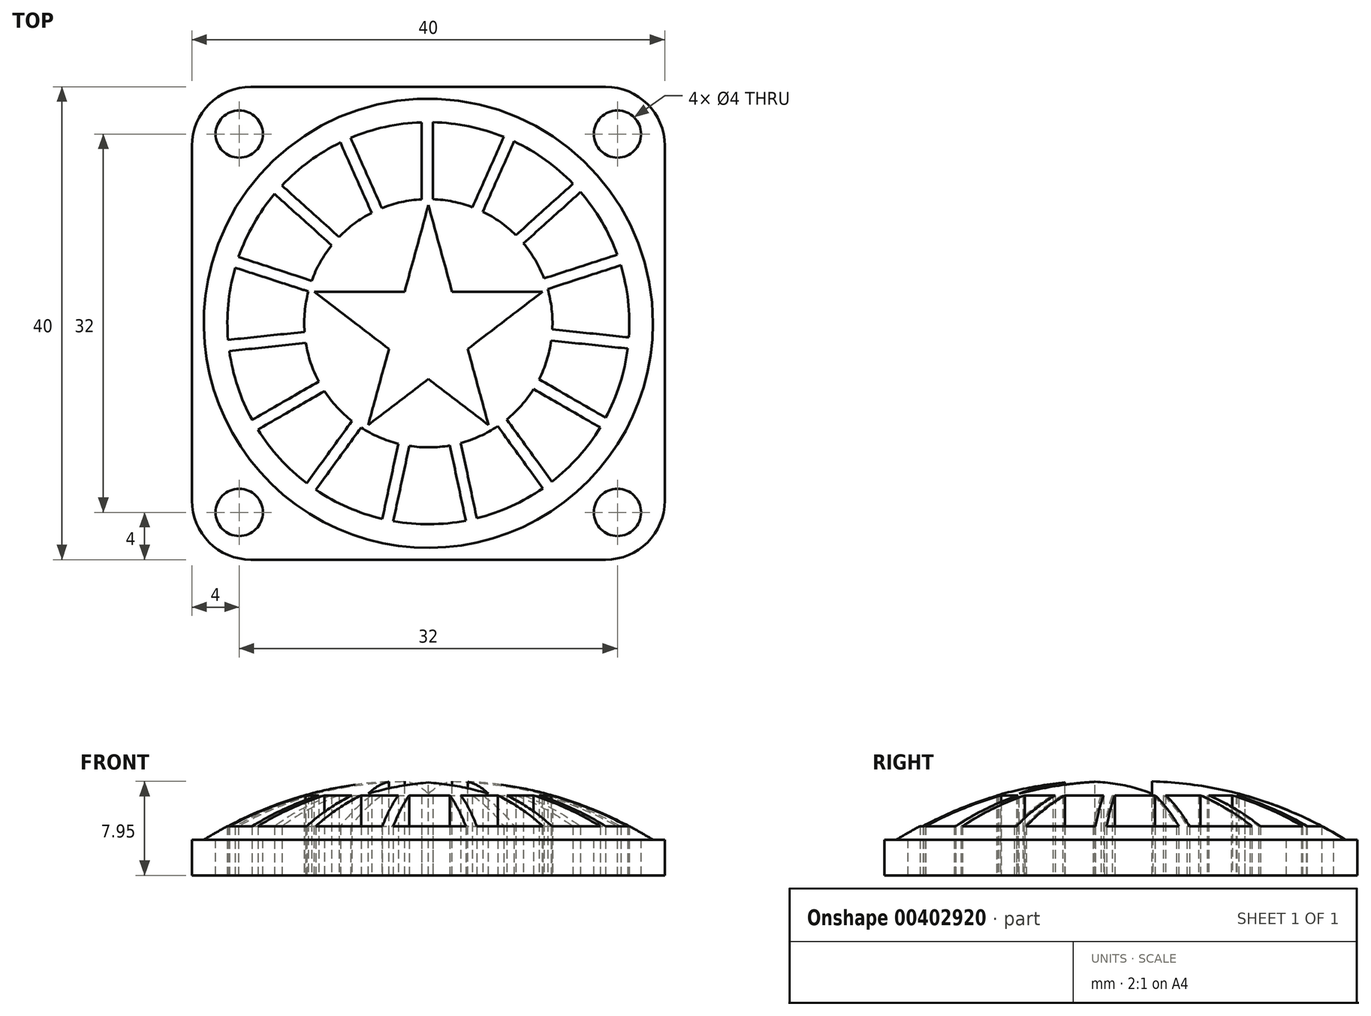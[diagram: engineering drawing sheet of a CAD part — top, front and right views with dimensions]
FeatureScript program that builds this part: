
annotation { "Feature Type Name" : "Feature", "Feature Type Description" : "" }
export const myFeature = defineFeature(function(context is Context, id is Id, definition is map)
    precondition{}
    {
        {
            var Q0;
            Q0=qCreatedBy(makeId("Top.planeOp"),FACE);
            var sketch = newSketch(context, id + "F0", { "sketchPlane" : qUnion([Q0])});
            skLineSegment(sketch, "E0.bottom", {"start": v(0, 0) * mm, "end": v(40, 0) * mm});
            skLineSegment(sketch, "E0.top", {"start": v(0, 40) * mm, "end": v(40, 40) * mm});
            skLineSegment(sketch, "E0.left", {"start": v(0, 0) * mm, "end": v(0, 40) * mm});
            skLineSegment(sketch, "E0.right", {"start": v(40, 0) * mm, "end": v(40, 40) * mm});
            skSolve(sketch);
        }
        {
            var Q0;
            Q0 = qSketchRegion(id + "F0", true);
            extrude(context, id + "F1", {"entities" : qUnion([Q0]), "depth" : 3 * mm, "offsetDistance" : 25 * mm});
        }
        {
            var Q0;
            Q0=makeQuery(id+"F1.opExtrude","CAP_FACE",FACE,{"disambiguationData":[OSD([sQuery(id+"F0.wireOp",EDGE,"E0.bottom"),sQuery(id+"F0.wireOp",EDGE,"E0.top"),sQuery(id+"F0.wireOp",EDGE,"E0.left"),sQuery(id+"F0.wireOp",EDGE,"E0.right")])],"isStart":false});
            var sketch = newSketch(context, id + "F2", { "sketchPlane" : qUnion([Q0])});
            skCircle(sketch, "E1", {"center": v(4, 36) * mm, "radius": 2 * mm});
            skCircle(sketch, "E2", {"center": v(36, 36) * mm, "radius": 2 * mm});
            skCircle(sketch, "E3", {"center": v(36, 4) * mm, "radius": 2 * mm});
            skCircle(sketch, "E4", {"center": v(4, 4) * mm, "radius": 2 * mm});
            skSolve(sketch);
        }
        {
            var Q0;
            Q0 = qSketchRegion(id + "F2", true);
            extrude(context, id + "F3", {"entities" : qUnion([Q0]), "operationType" : NewBodyOperationType.REMOVE, "oppositeDirection" : true, "depth" : 25 * mm, "offsetDistance" : 25 * mm});
        }
        {
            var Q0;
            Q0=makeQuery(id+"F1.opExtrude","CAP_FACE",FACE,{"disambiguationData":[OSD([sQuery(id+"F0.wireOp",EDGE,"E0.bottom"),sQuery(id+"F0.wireOp",EDGE,"E0.top"),sQuery(id+"F0.wireOp",EDGE,"E0.left"),sQuery(id+"F0.wireOp",EDGE,"E0.right")])],"isStart":false});
            var sketch = newSketch(context, id + "F4", { "sketchPlane" : qUnion([Q0])});
            skCircle(sketch, "E5", {"center": v(20, 20) * mm, "radius": 19 * mm});
            skPoint(sketch, "E5.centerSnap0", {"position": v(40, 20) * mm});
            skPoint(sketch, "E5.centerSnap1", {"position": v(20, 40) * mm});
            skSolve(sketch);
        }
        {
            var Q0;
            Q0 = qSketchRegion(id + "F4", true);
            extrude(context, id + "F5", {"entities" : qUnion([Q0]), "operationType" : NewBodyOperationType.ADD, "depth" : 5 * mm, "offsetDistance" : 25 * mm});
        }
        {
            var Q0;
            Q0=makeQuery(id+"F5.opExtrude","CAP_EDGE",EDGE,{"disambiguationData":[OSD([sQuery(id+"F4.wireOp",EDGE,"E5")])],"isStart":false});
            fillet(context, id + "F6", {"entities" : qUnion([Q0]), "radius" : 33 * mm, "tangentPropagation" : true, "allowEdgeOverflow" : false});
        }
        {
            var Q0;
            Q0=makeQuery(id+"F5.opExtrude","CAP_FACE",FACE,{"disambiguationData":[OSD([sQuery(id+"F4.wireOp",EDGE,"E5")])],"isStart":false});
            var sketch = newSketch(context, id + "F7", { "sketchPlane" : qUnion([Q0])});
            skLineSegment(sketch, "E6", {"start": v(20, 30) * mm, "end": v(17.99, 22.65) * mm});
            skLineSegment(sketch, "E7", {"start": v(25.1, 11.4) * mm, "end": v(20, 15.28) * mm});
            skLineSegment(sketch, "E8", {"start": v(10.36, 22.65) * mm, "end": v(17.99, 22.65) * mm});
            skLineSegment(sketch, "E9", {"start": v(29.64, 22.65) * mm, "end": v(23.33, 17.83) * mm});
            skLineSegment(sketch, "E10", {"start": v(20, 30) * mm, "end": v(22.01, 22.65) * mm});
            skLineSegment(sketch, "E11.trimOffspring", {"start": v(22.01, 22.65) * mm, "end": v(29.64, 22.65) * mm});
            skLineSegment(sketch, "E12.trimOffspring", {"start": v(16.67, 17.83) * mm, "end": v(14.9, 11.4) * mm});
            skLineSegment(sketch, "E13.trimOffspring", {"start": v(16.67, 17.83) * mm, "end": v(10.36, 22.65) * mm});
            skLineSegment(sketch, "E14.trimOffspring", {"start": v(20, 15.28) * mm, "end": v(14.9, 11.4) * mm});
            skLineSegment(sketch, "E15.trimOffspring", {"start": v(23.33, 17.83) * mm, "end": v(25.1, 11.4) * mm});
            skPoint(sketch, "E16.center.orphan", {"position": v(20, 20) * mm});
            skSolve(sketch);
        }
        {
            var Q0;
            Q0 = qSketchRegion(id + "F7", true);
            extrude(context, id + "F8", {"entities" : qUnion([Q0]), "operationType" : NewBodyOperationType.REMOVE, "oppositeDirection" : true, "depth" : 25 * mm, "offsetDistance" : 25 * mm});
        }
        {
            var Q0;
            Q0=makeQuery(id+"F1.opExtrude","CAP_FACE",FACE,{"disambiguationData":[OSD([sQuery(id+"F0.wireOp",EDGE,"E0.bottom"),sQuery(id+"F0.wireOp",EDGE,"E0.top"),sQuery(id+"F0.wireOp",EDGE,"E0.left"),sQuery(id+"F0.wireOp",EDGE,"E0.right")])],"isStart":true});
            var sketch = newSketch(context, id + "F9", { "sketchPlane" : qUnion([Q0])});
            skArc(sketch, "E17", {"start": v(20.37, -30.5) * mm, "mid": v(22.08, -30.3) * mm, "end": v(23.73, -29.81) * mm});
            skPoint(sketch, "E17.centerSnap0", {"position": v(20, -40) * mm});
            skPoint(sketch, "E17.centerSnap1", {"position": v(0, -20) * mm});
            skArc(sketch, "E18", {"start": v(20.37, -37) * mm, "mid": v(23.43, -36.65) * mm, "end": v(26.38, -35.76) * mm});
            skLineSegment(sketch, "E19.left", {"start": v(20.37, -37) * mm, "end": v(20.37, -30.48) * mm});
            skLineSegment(sketch, "E19.right", {"start": v(19.42, -37) * mm, "end": v(19.42, -30.48) * mm});
            skLineSegment(sketch, "E20.1.0", {"start": v(27.25, -35.38) * mm, "end": v(24.6, -29.43) * mm});
            skLineSegment(sketch, "E20.1.1", {"start": v(26.38, -35.76) * mm, "end": v(23.73, -29.81) * mm});
            skLineSegment(sketch, "E20.2.0", {"start": v(32.88, -31.1) * mm, "end": v(28.04, -26.74) * mm});
            skLineSegment(sketch, "E20.2.1", {"start": v(32.24, -31.8) * mm, "end": v(27.4, -27.45) * mm});
            skLineSegment(sketch, "E20.3.0", {"start": v(36.28, -24.9) * mm, "end": v(30.08, -22.89) * mm});
            skLineSegment(sketch, "E20.3.1", {"start": v(35.98, -25.8) * mm, "end": v(29.8, -23.8) * mm});
            skLineSegment(sketch, "E20.3.2", {"start": v(30.08, -22.89) * mm, "end": v(29.8, -23.8) * mm});
            skLineSegment(sketch, "E20.4.0", {"start": v(36.86, -17.86) * mm, "end": v(30.39, -18.54) * mm});
            skLineSegment(sketch, "E20.4.1", {"start": v(36.96, -18.8) * mm, "end": v(30.49, -19.48) * mm});
            skLineSegment(sketch, "E20.5.0", {"start": v(34.53, -11.18) * mm, "end": v(28.9, -14.44) * mm});
            skLineSegment(sketch, "E20.5.1", {"start": v(35, -12) * mm, "end": v(29.37, -15.26) * mm});
            skLineSegment(sketch, "E20.6.0", {"start": v(29.7, -6.03) * mm, "end": v(25.86, -11.3) * mm});
            skLineSegment(sketch, "E20.6.1", {"start": v(30.46, -6.6) * mm, "end": v(26.63, -11.86) * mm});
            skLineSegment(sketch, "E20.7.0", {"start": v(23.17, -3.3) * mm, "end": v(21.82, -9.67) * mm});
            skLineSegment(sketch, "E20.7.1", {"start": v(24.1, -3.5) * mm, "end": v(22.75, -9.87) * mm});
            skLineSegment(sketch, "E20.8.0", {"start": v(16.1, -3.45) * mm, "end": v(17.46, -9.82) * mm});
            skLineSegment(sketch, "E20.8.1", {"start": v(17.04, -3.26) * mm, "end": v(18.39, -9.62) * mm});
            skLineSegment(sketch, "E20.9.0", {"start": v(9.71, -6.47) * mm, "end": v(13.54, -11.74) * mm});
            skLineSegment(sketch, "E20.9.1", {"start": v(10.48, -5.91) * mm, "end": v(14.3, -11.18) * mm});
            skLineSegment(sketch, "E20.10.0", {"start": v(5.1, -11.82) * mm, "end": v(10.74, -15.08) * mm});
            skLineSegment(sketch, "E20.10.1", {"start": v(5.58, -11) * mm, "end": v(11.21, -14.25) * mm});
            skLineSegment(sketch, "E20.11.0", {"start": v(3.06, -18.6) * mm, "end": v(9.53, -19.27) * mm});
            skLineSegment(sketch, "E20.11.1", {"start": v(3.16, -17.65) * mm, "end": v(9.63, -18.33) * mm});
            skLineSegment(sketch, "E20.12.0", {"start": v(3.95, -25.6) * mm, "end": v(10.14, -23.6) * mm});
            skLineSegment(sketch, "E20.12.1", {"start": v(3.66, -24.7) * mm, "end": v(9.85, -22.69) * mm});
            skLineSegment(sketch, "E20.13.0", {"start": v(7.62, -31.65) * mm, "end": v(12.46, -27.29) * mm});
            skLineSegment(sketch, "E20.13.1", {"start": v(6.99, -30.94) * mm, "end": v(11.82, -26.58) * mm});
            skLineSegment(sketch, "E20.14.0", {"start": v(13.42, -35.68) * mm, "end": v(16.07, -29.73) * mm});
            skLineSegment(sketch, "E20.14.1", {"start": v(12.56, -35.28) * mm, "end": v(15.2, -29.34) * mm});
            skArc(sketch, "E21.trimOffspring", {"start": v(13.42, -35.68) * mm, "mid": v(16.36, -36.6) * mm, "end": v(19.42, -37) * mm});
            skArc(sketch, "E22.trimOffspring", {"start": v(16.07, -29.74) * mm, "mid": v(17.71, -30.25) * mm, "end": v(19.42, -30.48) * mm});
            skArc(sketch, "E23.trimOffspring", {"start": v(12.45, -27.3) * mm, "mid": v(13.74, -28.43) * mm, "end": v(15.2, -29.34) * mm});
            skArc(sketch, "E24.trimOffspring", {"start": v(7.62, -31.65) * mm, "mid": v(9.92, -33.7) * mm, "end": v(12.56, -35.28) * mm});
            skArc(sketch, "E25.trimOffspring", {"start": v(3.95, -25.6) * mm, "mid": v(5.22, -28.4) * mm, "end": v(6.99, -30.94) * mm});
            skArc(sketch, "E26.trimOffspring", {"start": v(10.13, -23.6) * mm, "mid": v(10.85, -25.16) * mm, "end": v(11.82, -26.58) * mm});
            skArc(sketch, "E27.trimOffspring", {"start": v(24.6, -29.44) * mm, "mid": v(26.09, -28.56) * mm, "end": v(27.4, -27.45) * mm});
            skArc(sketch, "E28.trimOffspring", {"start": v(27.25, -35.38) * mm, "mid": v(29.9, -33.82) * mm, "end": v(32.24, -31.8) * mm});
            skArc(sketch, "E29.trimOffspring", {"start": v(32.88, -31.1) * mm, "mid": v(34.67, -28.6) * mm, "end": v(35.98, -25.8) * mm});
            skArc(sketch, "E30.trimOffspring", {"start": v(28.05, -26.75) * mm, "mid": v(29.04, -25.34) * mm, "end": v(29.8, -23.8) * mm});
            skArc(sketch, "E31.trimOffspring", {"start": v(30.1, -22.9) * mm, "mid": v(30.43, -21.2) * mm, "end": v(30.49, -19.48) * mm});
            skArc(sketch, "E32.trimOffspring", {"start": v(36.28, -24.9) * mm, "mid": v(36.9, -21.88) * mm, "end": v(36.96, -18.8) * mm});
            skArc(sketch, "E33.trimOffspring", {"start": v(36.86, -17.86) * mm, "mid": v(36.2, -14.85) * mm, "end": v(35, -12) * mm});
            skArc(sketch, "E34.trimOffspring", {"start": v(30.4, -18.54) * mm, "mid": v(30.02, -16.86) * mm, "end": v(29.37, -15.26) * mm});
            skArc(sketch, "E35.trimOffspring", {"start": v(29.7, -6.03) * mm, "mid": v(27.01, -4.51) * mm, "end": v(24.1, -3.5) * mm});
            skArc(sketch, "E36.trimOffspring", {"start": v(34.53, -11.18) * mm, "mid": v(32.7, -8.7) * mm, "end": v(30.46, -6.6) * mm});
            skArc(sketch, "E37.trimOffspring", {"start": v(28.9, -14.43) * mm, "mid": v(27.87, -13.05) * mm, "end": v(26.63, -11.86) * mm});
            skArc(sketch, "E38.trimOffspring", {"start": v(25.87, -11.3) * mm, "mid": v(24.37, -10.45) * mm, "end": v(22.75, -9.87) * mm});
            skArc(sketch, "E39.trimOffspring", {"start": v(21.82, -9.66) * mm, "mid": v(20.1, -9.5) * mm, "end": v(18.39, -9.62) * mm});
            skArc(sketch, "E40.trimOffspring", {"start": v(23.17, -3.3) * mm, "mid": v(20.1, -3) * mm, "end": v(17.04, -3.26) * mm});
            skArc(sketch, "E41.trimOffspring", {"start": v(16.1, -3.45) * mm, "mid": v(13.18, -4.43) * mm, "end": v(10.48, -5.91) * mm});
            skArc(sketch, "E42.trimOffspring", {"start": v(17.46, -9.81) * mm, "mid": v(15.83, -10.37) * mm, "end": v(14.3, -11.18) * mm});
            skArc(sketch, "E43.trimOffspring", {"start": v(13.53, -11.73) * mm, "mid": v(12.27, -12.9) * mm, "end": v(11.21, -14.25) * mm});
            skArc(sketch, "E44.trimOffspring", {"start": v(9.71, -6.47) * mm, "mid": v(7.44, -8.55) * mm, "end": v(5.58, -11) * mm});
            skArc(sketch, "E45.trimOffspring", {"start": v(5.1, -11.82) * mm, "mid": v(3.87, -14.65) * mm, "end": v(3.16, -17.65) * mm});
            skArc(sketch, "E46.trimOffspring", {"start": v(10.73, -15.07) * mm, "mid": v(10.05, -16.65) * mm, "end": v(9.63, -18.33) * mm});
            skArc(sketch, "E47.trimOffspring", {"start": v(9.53, -19.27) * mm, "mid": v(9.55, -21) * mm, "end": v(9.85, -22.69) * mm});
            skArc(sketch, "E48.trimOffspring", {"start": v(3.06, -18.6) * mm, "mid": v(3.08, -21.67) * mm, "end": v(3.66, -24.7) * mm});
            skSolve(sketch);
        }
        {
            var Q0;
            Q0 = qSketchRegion(id + "F9", true);
            extrude(context, id + "F10", {"entities" : qUnion([Q0]), "operationType" : NewBodyOperationType.REMOVE, "oppositeDirection" : true, "depth" : 25 * mm, "offsetDistance" : 25 * mm});
        }
        {
            var Q0;
            Q0=makeQuery(id+"F1.opExtrude","SWEPT_EDGE",EDGE,{"disambiguationData":[OSD([sQuery(id+"F0.wireOp",EDGE,"E0.top"),sQuery(id+"F0.wireOp",EDGE,"E0.left")])]});
            fillet(context, id + "F11", {"entities" : qUnion([Q0]), "radius" : 5 * mm, "tangentPropagation" : true, "allowEdgeOverflow" : false});
        }
        {
            var Q0;
            Q0=makeQuery(id+"F1.opExtrude","SWEPT_EDGE",EDGE,{"disambiguationData":[OSD([sQuery(id+"F0.wireOp",EDGE,"E0.bottom"),sQuery(id+"F0.wireOp",EDGE,"E0.left")])]});
            fillet(context, id + "F12", {"entities" : qUnion([Q0]), "radius" : 5 * mm, "tangentPropagation" : true, "allowEdgeOverflow" : false});
        }
        {
            var Q0;
            Q0=makeQuery(id+"F1.opExtrude","SWEPT_EDGE",EDGE,{"disambiguationData":[OSD([sQuery(id+"F0.wireOp",EDGE,"E0.bottom"),sQuery(id+"F0.wireOp",EDGE,"E0.right")])]});
            fillet(context, id + "F13", {"entities" : qUnion([Q0]), "radius" : 5 * mm, "tangentPropagation" : true, "allowEdgeOverflow" : false});
        }
        {
            var Q0;
            Q0=makeQuery(id+"F1.opExtrude","SWEPT_EDGE",EDGE,{"disambiguationData":[OSD([sQuery(id+"F0.wireOp",EDGE,"E0.top"),sQuery(id+"F0.wireOp",EDGE,"E0.right")])]});
            fillet(context, id + "F14", {"entities" : qUnion([Q0]), "radius" : 5 * mm, "tangentPropagation" : true, "allowEdgeOverflow" : false});
        }
    });
